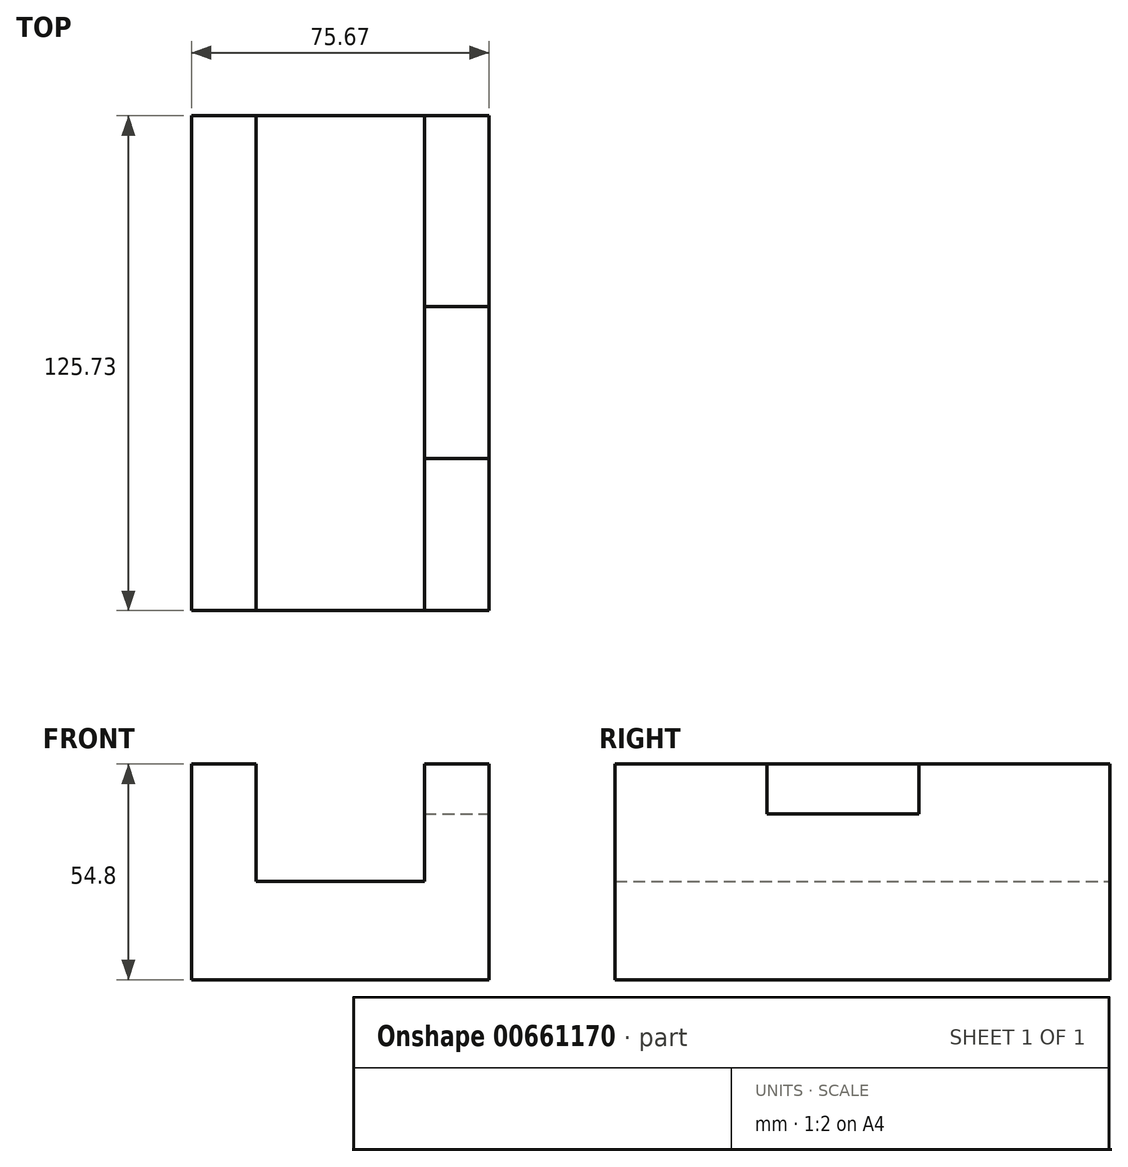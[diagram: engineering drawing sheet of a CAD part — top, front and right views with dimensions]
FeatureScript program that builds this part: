
annotation { "Feature Type Name" : "Feature", "Feature Type Description" : "" }
export const myFeature = defineFeature(function(context is Context, id is Id, definition is map)
    precondition{}
    {
        {
            var Q0;
            Q0=qCreatedBy(makeId("Front.planeOp"),FACE);
            var sketch = newSketch(context, id + "F0", { "sketchPlane" : qUnion([Q0])});
            skLineSegment(sketch, "E0.bottom", {"start": v(0, 0) * mm, "end": v(-75.67, 0) * mm});
            skLineSegment(sketch, "E0.top", {"start": v(0, 54.8) * mm, "end": v(-16.47, 54.8) * mm});
            skLineSegment(sketch, "E0.left", {"start": v(0, 0) * mm, "end": v(0, 54.8) * mm});
            skLineSegment(sketch, "E0.right", {"start": v(-75.67, 0) * mm, "end": v(-75.67, 54.8) * mm});
            skLineSegment(sketch, "E1.top", {"start": v(-59.2, 24.99) * mm, "end": v(-16.47, 24.99) * mm});
            skLineSegment(sketch, "E1.left", {"start": v(-59.2, 54.8) * mm, "end": v(-59.2, 24.99) * mm});
            skLineSegment(sketch, "E1.right", {"start": v(-16.47, 54.8) * mm, "end": v(-16.47, 24.99) * mm});
            skLineSegment(sketch, "E2.trimOffspring", {"start": v(-59.2, 54.8) * mm, "end": v(-75.67, 54.8) * mm});
            skSolve(sketch);
        }
        {
            var Q0;
            Q0=qSketchRegion(id+"F0",true);
            extrude(context, id + "F1", {"entities" : qUnion([Q0]), "depth" : 125.73 * mm, "offsetDistance" : 25.4 * mm});
        }
        {
            var Q0;
            Q0=makeQuery(id+"F1.opExtrude","SWEPT_FACE",FACE,{"disambiguationData":[OSD([sQuery(id+"F0.wireOp",EDGE,"E0.top")])]});
            var sketch = newSketch(context, id + "F2", { "sketchPlane" : qUnion([Q0])});
            skLineSegment(sketch, "E3.bottom", {"start": v(-16.47, -48.5) * mm, "end": v(0, -48.5) * mm});
            skLineSegment(sketch, "E3.top", {"start": v(-16.47, -87.11) * mm, "end": v(0, -87.11) * mm});
            skLineSegment(sketch, "E3.left", {"start": v(-16.47, -48.5) * mm, "end": v(-16.47, -87.11) * mm});
            skLineSegment(sketch, "E3.right", {"start": v(0, -48.5) * mm, "end": v(0, -87.11) * mm});
            skSolve(sketch);
        }
        {
            var Q0;
            Q0=qSketchRegion(id+"F2",true);
            extrude(context, id + "F3", {"entities" : qUnion([Q0]), "operationType" : NewBodyOperationType.REMOVE, "oppositeDirection" : true, "depth" : 12.7 * mm, "offsetDistance" : 25.4 * mm});
        }
    });
